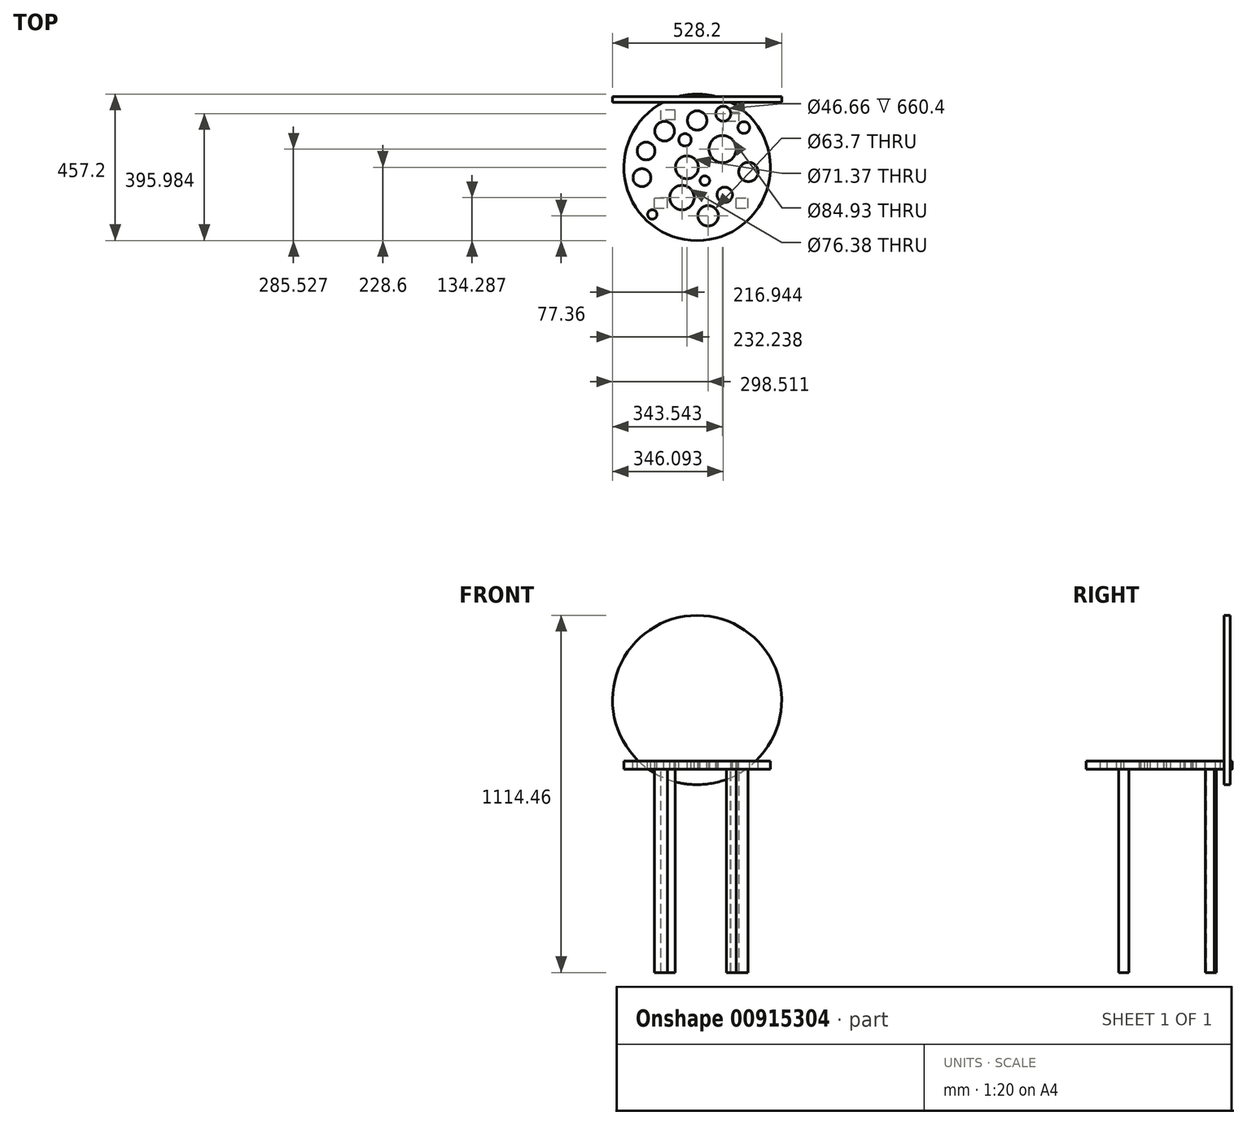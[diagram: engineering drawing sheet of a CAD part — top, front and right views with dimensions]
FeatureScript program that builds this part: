
annotation { "Feature Type Name" : "Feature", "Feature Type Description" : "" }
export const myFeature = defineFeature(function(context is Context, id is Id, definition is map)
    precondition{}
    {
        {
            var Q0;
            Q0=qCreatedBy(makeId("Top.planeOp"),FACE);
            var sketch = newSketch(context, id + "F0", { "sketchPlane" : qUnion([Q0])});
            skCircle(sketch, "E0", {"center": v(0, 0) * mm, "radius": 228.6 * mm});
            skSolve(sketch);
        }
        {
            var Q0;
            Q0=makeQuery(id+"F0.imprint","IMPRINT",FACE,{"disambiguationData":[TD([[makeQuery(id+"F0.imprint","IMPRINT",EDGE,{"derivedFrom":sQuery(id+"F0.wireOp",EDGE,"E0")}),1.0]])]});
            extrude(context, id + "F1", {"entities" : qUnion([Q0]), "depth" : 25.4 * mm, "offsetDistance" : 25.4 * mm});
        }
        {
            var Q0;
            Q0=makeQuery(id+"F1.opExtrude","CAP_FACE",FACE,{"disambiguationData":[OSD([sQuery(id+"F0.wireOp",EDGE,"E0")])],"isStart":true});
            var sketch = newSketch(context, id + "F2", { "sketchPlane" : qUnion([Q0])});
            skLineSegment(sketch, "E1.bottom", {"start": v(-132.97, 126.6) * mm, "end": v(-92.19, 126.6) * mm});
            skLineSegment(sketch, "E1.top", {"start": v(-132.97, 95.16) * mm, "end": v(-92.19, 95.16) * mm});
            skLineSegment(sketch, "E1.left", {"start": v(-132.97, 126.6) * mm, "end": v(-132.97, 95.16) * mm});
            skLineSegment(sketch, "E1.right", {"start": v(-92.19, 126.6) * mm, "end": v(-92.19, 95.16) * mm});
            skPoint(sketch, "E2.oppositeSnap0", {"position": v(-112.58, 95.16) * mm});
            skLineSegment(sketch, "E2.bottom", {"start": v(121.93, 126.6) * mm, "end": v(158.46, 126.6) * mm});
            skLineSegment(sketch, "E2.top", {"start": v(121.93, 95.16) * mm, "end": v(158.46, 95.16) * mm});
            skLineSegment(sketch, "E2.left", {"start": v(121.93, 126.6) * mm, "end": v(121.93, 95.16) * mm});
            skLineSegment(sketch, "E2.right", {"start": v(158.46, 126.6) * mm, "end": v(158.46, 95.16) * mm});
            skLineSegment(sketch, "E3.bottom", {"start": v(91.34, -144.44) * mm, "end": v(131.27, -144.44) * mm});
            skLineSegment(sketch, "E3.top", {"start": v(91.34, -172.48) * mm, "end": v(131.27, -172.48) * mm});
            skLineSegment(sketch, "E3.left", {"start": v(91.34, -144.44) * mm, "end": v(91.34, -172.48) * mm});
            skLineSegment(sketch, "E3.right", {"start": v(131.27, -144.44) * mm, "end": v(131.27, -172.48) * mm});
            skLineSegment(sketch, "E4.bottom", {"start": v(-68.4, -147.84) * mm, "end": v(-112.58, -147.84) * mm});
            skLineSegment(sketch, "E4.top", {"start": v(-68.4, -178.43) * mm, "end": v(-112.58, -178.43) * mm});
            skLineSegment(sketch, "E4.left", {"start": v(-68.4, -147.84) * mm, "end": v(-68.4, -178.43) * mm});
            skLineSegment(sketch, "E4.right", {"start": v(-112.58, -147.84) * mm, "end": v(-112.58, -178.43) * mm});
            skSolve(sketch);
        }
        {
            var Q0;
            Q0 = qSketchRegion(id + "F2", true);
            extrude(context, id + "F3", {"entities" : qUnion([Q0]), "operationType" : NewBodyOperationType.ADD, "depth" : 635 * mm, "offsetDistance" : 25.4 * mm});
        }
        {
            var Q0;
            Q0=makeQuery(id+"F1.opExtrude","CAP_FACE",FACE,{"disambiguationData":[OSD([sQuery(id+"F0.wireOp",EDGE,"E0")])],"isStart":false});
            var sketch = newSketch(context, id + "F4", { "sketchPlane" : qUnion([Q0])});
            skCircle(sketch, "E5", {"center": v(-159.31, 50.98) * mm, "radius": 27.74 * mm});
            skCircle(sketch, "E6", {"center": v(-101.53, 113) * mm, "radius": 30.7 * mm});
            skCircle(sketch, "E7", {"center": v(0, 146.14) * mm, "radius": 30.28 * mm});
            skCircle(sketch, "E8", {"center": v(79.44, 56.93) * mm, "radius": 42.47 * mm});
            skCircle(sketch, "E9", {"center": v(-31.86, 0) * mm, "radius": 35.69 * mm});
            skCircle(sketch, "E10", {"center": v(86.24, -85.82) * mm, "radius": 24.03 * mm});
            skCircle(sketch, "E11", {"center": v(-47.16, -94.31) * mm, "radius": 38.19 * mm});
            skCircle(sketch, "E12", {"center": v(-172.06, -32.29) * mm, "radius": 27.87 * mm});
            skCircle(sketch, "E13", {"center": v(160.16, -14.44) * mm, "radius": 30.17 * mm});
            skCircle(sketch, "E14", {"center": v(145.72, 124.05) * mm, "radius": 18.3 * mm});
            skCircle(sketch, "E15", {"center": v(34.41, -151.24) * mm, "radius": 31.85 * mm});
            skCircle(sketch, "E16", {"center": v(-139.77, -147) * mm, "radius": 14.62 * mm});
            skCircle(sketch, "E17", {"center": v(24.22, -41.63) * mm, "radius": 14.86 * mm});
            skCircle(sketch, "E18", {"center": v(-37.81, 85.82) * mm, "radius": 19.4 * mm});
            skCircle(sketch, "E19", {"center": v(82, 167.38) * mm, "radius": 23.33 * mm});
            skSolve(sketch);
        }
        {
            var Q0;
            Q0 = qSketchRegion(id + "F4", true);
            extrude(context, id + "F5", {"entities" : qUnion([Q0]), "operationType" : NewBodyOperationType.REMOVE, "oppositeDirection" : true, "depth" : 977.9 * mm, "offsetDistance" : 25.4 * mm});
        }
        {
            var Q0;
            Q0=qCreatedBy(makeId("Front.planeOp"),FACE);
            var sketch = newSketch(context, id + "F6", { "sketchPlane" : qUnion([Q0])});
            skCircle(sketch, "E20", {"center": v(0, 215.36) * mm, "radius": 264.1 * mm});
            skSolve(sketch);
        }
        {
            var Q0;
            Q0=makeQuery(id+"F6.imprint","IMPRINT",FACE,{"disambiguationData":[TD([[makeQuery(id+"F6.imprint","IMPRINT",EDGE,{"derivedFrom":sQuery(id+"F6.wireOp",EDGE,"E20")}),1.0]])]});
            extrude(context, id + "F7", {"entities" : qUnion([Q0]), "operationType" : NewBodyOperationType.ADD, "oppositeDirection" : true, "depth" : 220.98 * mm, "offsetDistance" : 25.4 * mm, "hasSecondDirection" : true, "secondDirectionOppositeDirection" : true, "secondDirectionDepth" : 203.2 * mm});
        }
    });
